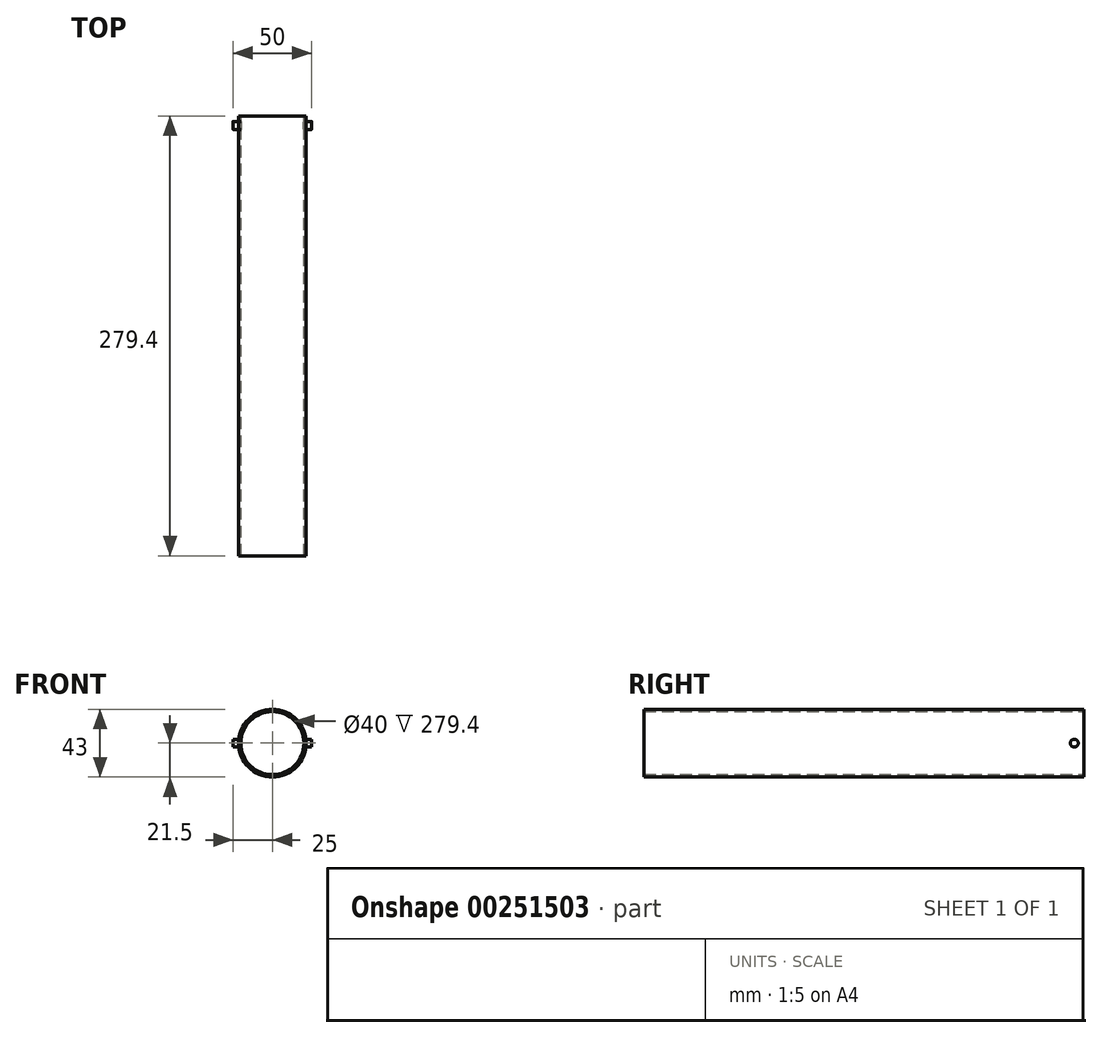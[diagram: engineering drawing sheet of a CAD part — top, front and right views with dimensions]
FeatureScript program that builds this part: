
annotation { "Feature Type Name" : "Feature", "Feature Type Description" : "" }
export const myFeature = defineFeature(function(context is Context, id is Id, definition is map)
    precondition{}
    {
        {
            var Q0;
            Q0=qCreatedBy(makeId("Right.planeOp"),FACE);
            var sketch = newSketch(context, id + "F0", { "sketchPlane" : qUnion([Q0])});
            skCircle(sketch, "E0", {"center": v(-6.05, 0) * mm, "radius": 2.5 * mm});
            skSolve(sketch);
        }
        {
            var Q0;
            Q0 = qSketchRegion(id + "F0", true);
            extrude(context, id + "F1", {"entities" : qUnion([Q0]), "endBound" : BoundingType.SYMMETRIC, "depth" : 50 * mm});
        }
        {
            var Q0;
            Q0=qCreatedBy(makeId("Front.planeOp"),FACE);
            var sketch = newSketch(context, id + "F2", { "sketchPlane" : qUnion([Q0])});
            skCircle(sketch, "E1", {"center": v(0, 0) * mm, "radius": 20 * mm});
            skLineSegment(sketch, "E2", {"start": v(0, 20) * mm, "end": v(0, -20) * mm});
            skCircle(sketch, "E3", {"center": v(0, 0) * mm, "radius": 21.5 * mm});
            skSolve(sketch);
        }
        {
            var Q0;
            Q0 = qSketchRegion(id + "F2", true);
            extrude(context, id + "F3", {"entities" : qUnion([Q0]), "depth" : 279.4 * mm});
        }
        {
            var Q0;
            Q0=qCreatedBy(makeId("Front.planeOp"),FACE);
            var sketch = newSketch(context, id + "F4", { "sketchPlane" : qUnion([Q0])});
            skCircle(sketch, "E4", {"center": v(0, 0) * mm, "radius": 20 * mm});
            skSolve(sketch);
        }
        {
            var Q0;
            Q0=makeQuery(id+"F4.imprint","IMPRINT",FACE,{"disambiguationData":[TD([[makeQuery(id+"F4.imprint","IMPRINT",EDGE,{"derivedFrom":sQuery(id+"F4.wireOp",EDGE,"E4")}),1.0]])]});
            extrude(context, id + "F5", {"entities" : qUnion([Q0]), "operationType" : NewBodyOperationType.REMOVE, "depth" : 21.34 * mm});
        }
    });
